# Revit family: Prises non verrouillées saillies 20_25V
name_source: partatom
category: Installations électriques
revit_build: Autodesk Revit 2018 (Build: 20170223_1515(x64)
units: mm (PartAtom-declared; Revit-internal decimal feet)

## family parameters
Conserver l'orientation des annotations = Non
Cote de connecteur circulaire = Utiliser le diamètre
Couper avec des vides une fois chargée = Non
Hôte = Face
Partagée = Non
Point de calcul de pièce = Non
Type d'élément = Normal

## types (3) — shared parameters
Couleur caractéristique = violet
Diamètre entrée de câble = M25
Elévation par défaut = 1000 mm  [stored 3.28084 ft]
Fabricant = Legrand
Famille produit = 0854-P17 TEMPRA PRO
Nombre de pôles = 2
Prise au standard international pour montage encastré ou saillie avec accessoire permet la connexion d'appareils de puissance = Prise au standard international pour montage encastré ou saillie avec accessoire permet la connexion d'appareils de puissance
Standard CEI ou NFC = CEI
Température maximum d'utilisation = 40
Température minimum d'utilisation = -25
Tension V = 20 25 V  50/60 Hz  violet
Type de cerrouillage = x
classe de protection IP = IP44
entraxe de fixation horizontal mm = 73 mm
entraxe de fixation vertical mm = 72 mm
hauteur mm = 103 mm  [stored 0.337927 ft]
largeur mm = 84 mm  [stored 0.275591 ft]
matériau du boitier = plastique
profondeur mm = 101 mm  [stored 0.331365 ft]
résistance aux chocs IK = 9
sans halogène = Oui
type de raccordement = bornes à vis
zero-valued in all types: Position de la Terre h

## per-type parameters (varying)
| type | Description | Intensité A | Modèle |
| IDS_LG_055206 | IDS_DESCRIPTION_LG_055206 | 16 A | LG-055206 |
| IDS_LG_055207 | IDS_DESCRIPTION_LG_055207 | 16 A | LG-055207 |
| IDS_LG_055256 | IDS_DESCRIPTION_LG_055256 | 32 A | LG-055256 |

note: [stored X ft] marks values corroborated as IEEE doubles in the binary element streams (Revit-internal decimal feet)
